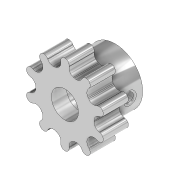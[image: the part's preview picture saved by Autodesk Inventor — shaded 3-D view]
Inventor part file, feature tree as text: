
AUTODESK INVENTOR PART (.ipt)
format: ipt  version: 2020 (Build 240168000, 168)  size: 414,208 bytes
history: native  units: in
note: dims shown in document units (in); Inventor stores cm internally (conversion verified against a paired STEP export)
features: extrude x4, sketch x4, chamfer x1, fillet x1, projected_geometry x1
ambient origin geometry x8: Origin, YZ Plane, XZ Plane, XY Plane, X Axis, Y Axis, Z Axis, Center Point
bodies: Body1 (feature_tree)
feature tree (11):
  extrude  "Extrusion4"  Depth=0.1969in
  extrude  "Extrusion5"  Depth=0.0866in
  extrude  "Extrusion6"  Depth=0.0827in
  extrude  "Extrusion7"  Depth=3.937in TaperAngle=360.0deg
  chamfer  "Chamfer2"  Distance=0.1969in
  fillet  "Fillet3"  Radius=0.1181in
  sketch  "Sketch4"  dims[d1=0.563in d2=0.0866in d19=0.1969in]
  sketch  "Sketch5"  dims[d20=0.6457in d21=0.0866in]
  sketch  "Sketch6"  dims[d22=0.0827in d23=0.0827in]
  sketch  "Sketch7"  dims[d24=0.0827in d25=3.937in d27=360.0deg d29=0.1969in d30=0.0in d31=0.1181in d32=0.1969in d33=0.0in d34=0.0748in d35=0.1969in d36=0.0in d42=0.0079in d43=0.0079in d44=1.0in d45=0.0in d46=0.2756in d47=0.125in d48=0.0137in d49=0.0118in]
  projected_geometry  "Projected Loop1"
